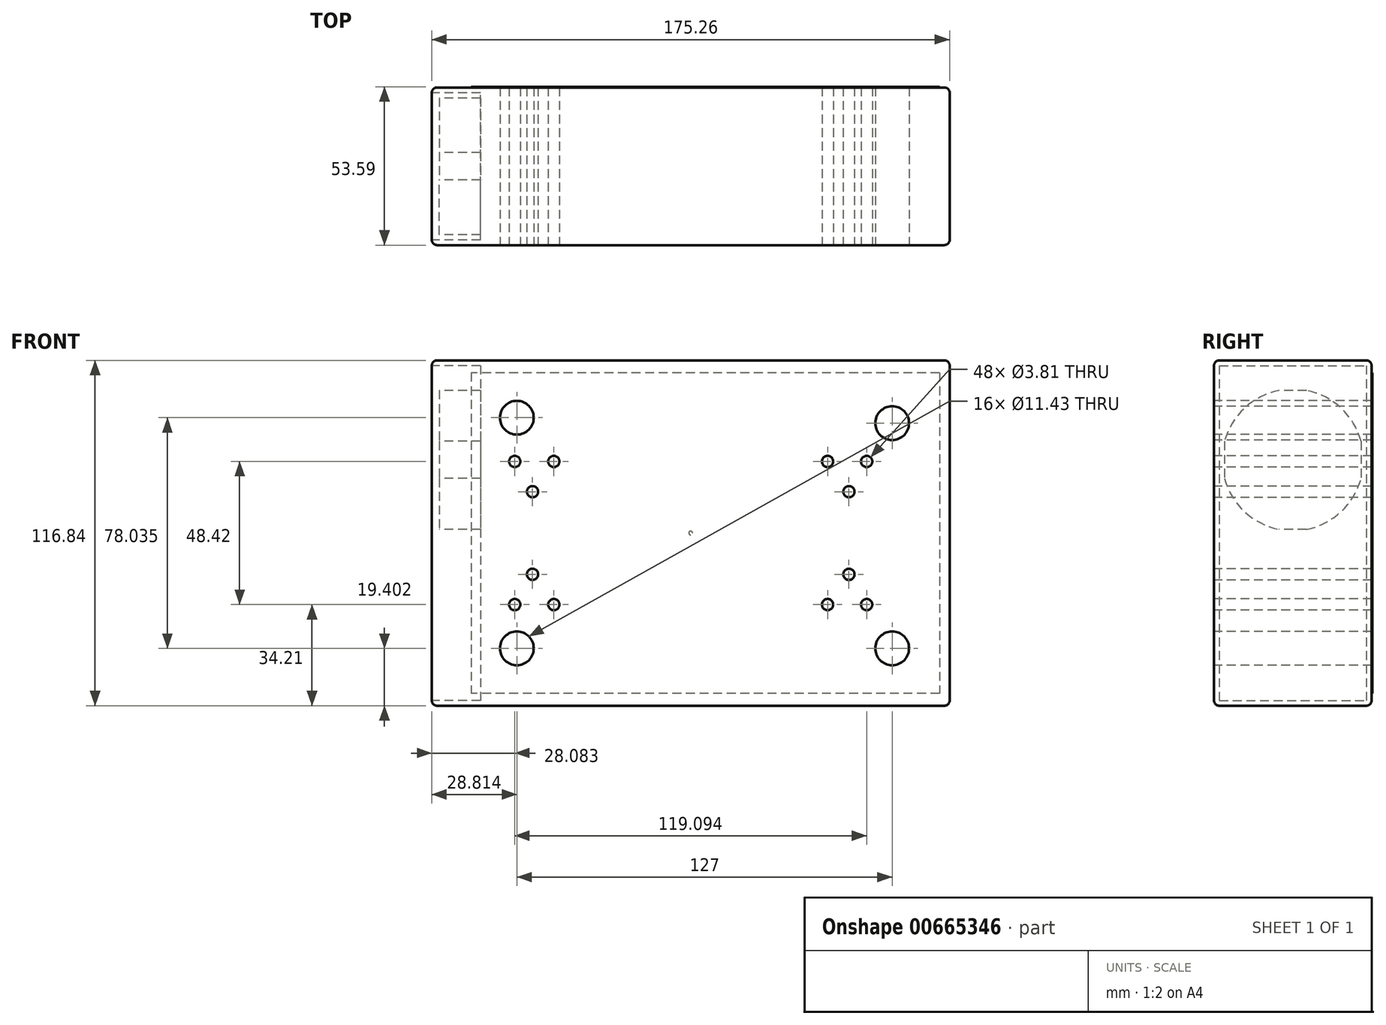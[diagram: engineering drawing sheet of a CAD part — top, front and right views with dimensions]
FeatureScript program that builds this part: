
annotation { "Feature Type Name" : "Feature", "Feature Type Description" : "" }
export const myFeature = defineFeature(function(context is Context, id is Id, definition is map)
    precondition{}
    {
        {
            var Q0;
            Q0=qCreatedBy(makeId("Front.planeOp"),FACE);
            var sketch = newSketch(context, id + "F0", { "sketchPlane" : qUnion([Q0])});
            skLineSegment(sketch, "E0.bottom", {"start": v(-87.63, 58.42) * mm, "end": v(87.63, 58.42) * mm});
            skLineSegment(sketch, "E0.top", {"start": v(-87.63, -58.42) * mm, "end": v(87.63, -58.42) * mm});
            skLineSegment(sketch, "E0.left", {"start": v(-87.63, 58.42) * mm, "end": v(-87.63, -58.42) * mm});
            skLineSegment(sketch, "E0.right", {"start": v(87.63, 58.42) * mm, "end": v(87.63, -58.42) * mm});
            skPoint(sketch, "E0.middle", {"position": v(0, 0) * mm});
            skSolve(sketch);
        }
        {
            var Q0;
            Q0=makeQuery(id+"F0.imprint","IMPRINT",FACE,{"disambiguationData":[TD([[makeQuery(id+"F0.imprint","IMPRINT",EDGE,{"derivedFrom":sQuery(id+"F0.wireOp",EDGE,"E0.bottom")}),-1.0]])]});
            extrude(context, id + "F1", {"entities" : qUnion([Q0]), "depth" : 53.34 * mm});
        }
        {
            var Q0;
            Q0=makeQuery(id+"F1.opExtrude","CAP_FACE",FACE,{"disambiguationData":[OSD([sQuery(id+"F0.wireOp",EDGE,"E0.bottom"),sQuery(id+"F0.wireOp",EDGE,"E0.top"),sQuery(id+"F0.wireOp",EDGE,"E0.left"),sQuery(id+"F0.wireOp",EDGE,"E0.right")])],"isStart":true});
            var sketch = newSketch(context, id + "F2", { "sketchPlane" : qUnion([Q0])});
            skLineSegment(sketch, "E1", {"start": v(-87.63, 54.2) * mm, "end": v(87.63, 54.2) * mm});
            skLineSegment(sketch, "E2.MirrorCS", {"start": v(-87.63, -54.2) * mm, "end": v(87.63, -54.2) * mm});
            skLineSegment(sketch, "E3", {"start": v(74.22, 58.42) * mm, "end": v(74.22, -58.42) * mm});
            skLineSegment(sketch, "E4", {"start": v(-84.2, 54.2) * mm, "end": v(-84.2, -58.42) * mm});
            skCircle(sketch, "E5", {"center": v(0, 0) * mm, "radius": 0.64 * mm});
            skSolve(sketch);
        }
        {
            var Q0;
            Q0=qSketchRegion(id+"F2",true);
            extrude(context, id + "F3", {"entities" : qUnion([Q0]), "depth" : 0.25 * mm});
        }
        {
            var Q0;
            Q0=makeQuery(id+"F1.opExtrude","CAP_FACE",FACE,{"disambiguationData":[OSD([sQuery(id+"F0.wireOp",EDGE,"E0.bottom"),sQuery(id+"F0.wireOp",EDGE,"E0.top"),sQuery(id+"F0.wireOp",EDGE,"E0.left"),sQuery(id+"F0.wireOp",EDGE,"E0.right")])],"isStart":false});
            var sketch = newSketch(context, id + "F4", { "sketchPlane" : qUnion([Q0])});
            skCircle(sketch, "E6", {"center": v(68.18, -39.02) * mm, "radius": 4.35 * mm});
            skCircle(sketch, "E7", {"center": v(-58.82, -39.02) * mm, "radius": 4.87 * mm});
            skCircle(sketch, "E8", {"center": v(68.18, 37.18) * mm, "radius": 4.37 * mm});
            skCircle(sketch, "E9.MirrorC", {"center": v(-58.82, 39.02) * mm, "radius": 4.87 * mm});
            skCircle(sketch, "E10", {"center": v(59.55, -24.2) * mm, "radius": 1.93 * mm});
            skCircle(sketch, "E11", {"center": v(53.53, -13.98) * mm, "radius": 1.7 * mm});
            skCircle(sketch, "E12", {"center": v(46.31, -24.2) * mm, "radius": 1.93 * mm});
            skCircle(sketch, "E13.MirrorC", {"center": v(59.55, 24.2) * mm, "radius": 1.93 * mm});
            skCircle(sketch, "E14.MirrorC", {"center": v(46.31, 24.2) * mm, "radius": 1.93 * mm});
            skCircle(sketch, "E15.MirrorC", {"center": v(53.53, 13.98) * mm, "radius": 1.7 * mm});
            skCircle(sketch, "E16.MirrorC", {"center": v(-46.31, -24.2) * mm, "radius": 1.93 * mm});
            skCircle(sketch, "E17.MirrorC", {"center": v(-59.55, -24.2) * mm, "radius": 1.93 * mm});
            skCircle(sketch, "E18.MirrorC", {"center": v(-53.53, -13.98) * mm, "radius": 1.7 * mm});
            skCircle(sketch, "E19.MirrorC", {"center": v(-46.31, 24.2) * mm, "radius": 1.93 * mm});
            skCircle(sketch, "E20.MirrorC", {"center": v(-53.53, 13.98) * mm, "radius": 1.7 * mm});
            skCircle(sketch, "E21.MirrorC", {"center": v(-59.55, 24.2) * mm, "radius": 1.93 * mm});
            skSolve(sketch);
        }
        {
            var Q0;
            Q0=sQuery(id+"F4.wireOp",VERTEX,"E6.center");
            var Q1;
            Q1=sQuery(id+"F4.wireOp",VERTEX,"E8.center");
            var Q2;
            Q2=sQuery(id+"F4.wireOp",VERTEX,"E7.center");
            var Q3;
            Q3=sQuery(id+"F4.wireOp",VERTEX,"E9.MirrorC.center");
            var Q4;
            Q4=makeQuery(id+"F1.opExtrude","SWEPT_BODY",BODY,{"disambiguationData":[OSD([sQuery(id+"F0.wireOp",EDGE,"E0.bottom"),sQuery(id+"F0.wireOp",EDGE,"E0.top"),sQuery(id+"F0.wireOp",EDGE,"E0.left"),sQuery(id+"F0.wireOp",EDGE,"E0.right")])]});
            var Q5;
            Q5=makeQuery(id+"F3.opExtrude","SWEPT_BODY",BODY,{"disambiguationData":[OSD([sQuery(id+"F2.wireOp",EDGE,"E1"),sQuery(id+"F2.wireOp",EDGE,"E2.MirrorCS"),sQuery(id+"F2.wireOp",EDGE,"E3"),sQuery(id+"F2.wireOp",EDGE,"E4")])]});
            hole(context, id + "F5", {"style" : HoleStyle.SIMPLE, "endStyle" : HoleEndStyle.BLIND_IN_LAST, "holeDiameter" : 11.43 * mm, "tapDrillDiameter" : 11.43 * mm, "holeDepth" : 12.7 * mm, "locations" : qUnion([Q0, Q1, Q2, Q3]), "scope" : qUnion([Q4, Q5])});
        }
        {
            var Q0;
            Q0=sQuery(id+"F4.wireOp",VERTEX,"E10.center");
            var Q1;
            Q1=sQuery(id+"F4.wireOp",VERTEX,"E11.center");
            var Q2;
            Q2=sQuery(id+"F4.wireOp",VERTEX,"E12.center");
            var Q3;
            Q3=sQuery(id+"F4.wireOp",VERTEX,"E15.MirrorC.center");
            var Q4;
            Q4=sQuery(id+"F4.wireOp",VERTEX,"E14.MirrorC.center");
            var Q5;
            Q5=sQuery(id+"F4.wireOp",VERTEX,"E13.MirrorC.center");
            var Q6;
            Q6=sQuery(id+"F4.wireOp",VERTEX,"E18.MirrorC.center");
            var Q7;
            Q7=sQuery(id+"F4.wireOp",VERTEX,"E17.MirrorC.center");
            var Q8;
            Q8=sQuery(id+"F4.wireOp",VERTEX,"E16.MirrorC.center");
            var Q9;
            Q9=sQuery(id+"F4.wireOp",VERTEX,"E20.MirrorC.center");
            var Q10;
            Q10=sQuery(id+"F4.wireOp",VERTEX,"E21.MirrorC.center");
            var Q11;
            Q11=sQuery(id+"F4.wireOp",VERTEX,"E19.MirrorC.center");
            var Q12;
            Q12=makeQuery(id+"F1.opExtrude","SWEPT_BODY",BODY,{"disambiguationData":[OSD([sQuery(id+"F0.wireOp",EDGE,"E0.bottom"),sQuery(id+"F0.wireOp",EDGE,"E0.top"),sQuery(id+"F0.wireOp",EDGE,"E0.left"),sQuery(id+"F0.wireOp",EDGE,"E0.right")])]});
            var Q13;
            Q13=makeQuery(id+"F3.opExtrude","SWEPT_BODY",BODY,{"disambiguationData":[OSD([sQuery(id+"F2.wireOp",EDGE,"E1"),sQuery(id+"F2.wireOp",EDGE,"E2.MirrorCS"),sQuery(id+"F2.wireOp",EDGE,"E3"),sQuery(id+"F2.wireOp",EDGE,"E4")])]});
            hole(context, id + "F6", {"style" : HoleStyle.SIMPLE, "endStyle" : HoleEndStyle.BLIND_IN_LAST, "holeDiameter" : 3.8 * mm, "tapDrillDiameter" : 3.8 * mm, "holeDepth" : 12.7 * mm, "locations" : qUnion([Q0, Q1, Q2, Q3, Q4, Q5, Q6, Q7, Q8, Q9, Q10, Q11]), "scope" : qUnion([Q12, Q13])});
        }
        {
            var Q0;
            Q0=makeQuery(id+"F1.opExtrude","SWEPT_FACE",FACE,{"disambiguationData":[OSD([sQuery(id+"F0.wireOp",EDGE,"E0.left")])]});
            var Q1;
            Q1=makeQuery(id+"F1.opExtrude","SWEPT_FACE",FACE,{"disambiguationData":[OSD([sQuery(id+"F0.wireOp",EDGE,"E0.bottom")])]});
            var Q2;
            Q2=makeQuery(id+"F1.opExtrude","SWEPT_FACE",FACE,{"disambiguationData":[OSD([sQuery(id+"F0.wireOp",EDGE,"E0.right")])]});
            var Q3;
            Q3=makeQuery(id+"F1.opExtrude","SWEPT_FACE",FACE,{"disambiguationData":[OSD([sQuery(id+"F0.wireOp",EDGE,"E0.top")])]});
            fillet(context, id + "F7", {"entities" : qUnion([Q0, Q1, Q2, Q3]), "radius" : 1.78 * mm, "tangentPropagation" : true, "allowEdgeOverflow" : false});
        }
        {
            var Q0;
            Q0=makeQuery(id+"F1.opExtrude","SWEPT_FACE",FACE,{"disambiguationData":[OSD([sQuery(id+"F0.wireOp",EDGE,"E0.left")])]});
            var sketch = newSketch(context, id + "F8", { "sketchPlane" : qUnion([Q0])});
            skLineSegment(sketch, "E22", {"start": v(1.78, 0) * mm, "end": v(51.56, 0) * mm, "construction": true});
            skLineSegment(sketch, "E23", {"start": v(26.67, -56.64) * mm, "end": v(26.67, 56.64) * mm, "construction": true});
            skPoint(sketch, "E24.middle", {"position": v(26.67, -29.91) * mm});
            skArc(sketch, "E25", {"start": v(31.33, -48.24) * mm, "mid": v(43.02, -42.25) * mm, "end": v(49.79, -31.01) * mm});
            skLineSegment(sketch, "E26.bottom", {"start": v(22, -48.24) * mm, "end": v(31.33, -48.24) * mm});
            skLineSegment(sketch, "E26.top", {"start": v(22, -1.25) * mm, "end": v(31.33, -1.25) * mm});
            skLineSegment(sketch, "E26.left", {"start": v(3.55, -31.01) * mm, "end": v(3.55, -18.48) * mm});
            skLineSegment(sketch, "E26.right", {"start": v(49.79, -31.01) * mm, "end": v(49.79, -18.48) * mm});
            skPoint(sketch, "E27.orphan", {"position": v(3.55, -48.24) * mm});
            skPoint(sketch, "E28.orphan", {"position": v(49.79, -48.24) * mm});
            skArc(sketch, "E29.trimOffspring", {"start": v(3.55, -31.01) * mm, "mid": v(10.32, -42.25) * mm, "end": v(22, -48.24) * mm});
            skPoint(sketch, "E30.orphan", {"position": v(3.55, -1.25) * mm});
            skArc(sketch, "E31.trimOffspring", {"start": v(22, -1.25) * mm, "mid": v(10.32, -7.23) * mm, "end": v(3.55, -18.48) * mm});
            skPoint(sketch, "E32.orphan", {"position": v(49.79, -1.25) * mm});
            skArc(sketch, "E33.trimOffspring", {"start": v(49.79, -18.48) * mm, "mid": v(43.02, -7.23) * mm, "end": v(31.33, -1.25) * mm});
            skArc(sketch, "E34.MirrorCS", {"start": v(22, 1.25) * mm, "mid": v(10.32, 7.23) * mm, "end": v(3.55, 18.48) * mm});
            skLineSegment(sketch, "E35.MirrorCS", {"start": v(22, 1.25) * mm, "end": v(31.33, 1.25) * mm});
            skArc(sketch, "E36.MirrorCS", {"start": v(49.79, 18.48) * mm, "mid": v(43.02, 7.23) * mm, "end": v(31.33, 1.25) * mm});
            skLineSegment(sketch, "E37.MirrorCS", {"start": v(49.79, 31.01) * mm, "end": v(49.79, 18.48) * mm});
            skArc(sketch, "E38.MirrorCS", {"start": v(31.33, 48.24) * mm, "mid": v(43.02, 42.25) * mm, "end": v(49.79, 31.01) * mm});
            skLineSegment(sketch, "E39.MirrorCS", {"start": v(22, 48.24) * mm, "end": v(31.33, 48.24) * mm});
            skArc(sketch, "E40.MirrorCS", {"start": v(3.55, 31.01) * mm, "mid": v(10.32, 42.25) * mm, "end": v(22, 48.24) * mm});
            skLineSegment(sketch, "E41.MirrorCS", {"start": v(3.55, 31.01) * mm, "end": v(3.55, 18.48) * mm});
            skSolve(sketch);
        }
        {
            var Q0;
            Q0=makeQuery(id+"F8.imprint","IMPRINT",FACE,{"disambiguationData":[TD([[makeQuery(id+"F8.imprint","IMPRINT",EDGE,{"derivedFrom":sQuery(id+"F8.wireOp",EDGE,"E25")}),1.0]])]});
            var Q1;
            Q1=makeQuery(id+"F8.imprint","IMPRINT",FACE,{"disambiguationData":[TD([[makeQuery(id+"F8.imprint","IMPRINT",EDGE,{"derivedFrom":sQuery(id+"F8.wireOp",EDGE,"E34.MirrorCS")}),-1.0]])]});
            extrude(context, id + "F9", {"entities" : qUnion([Q0, Q1]), "operationType" : NewBodyOperationType.REMOVE, "oppositeDirection" : true, "depth" : 16.5 * mm});
        }
        {
            var Q0;
            Q0=makeQuery(id+"F1.opExtrude","SWEPT_FACE",FACE,{"disambiguationData":[OSD([sQuery(id+"F0.wireOp",EDGE,"E0.left")])]});
            var sketch = newSketch(context, id + "F10", { "sketchPlane" : qUnion([Q0])});
            skCircle(sketch, "E42", {"center": v(8.88, -51.96) * mm, "radius": 3.43 * mm});
            skLineSegment(sketch, "E43.0", {"start": v(7.32, -51.96) * mm, "end": v(8.1, -50.6) * mm});
            skLineSegment(sketch, "E43.1", {"start": v(8.1, -50.6) * mm, "end": v(9.74, -50.57) * mm});
            skLineSegment(sketch, "E43.2", {"start": v(9.74, -50.57) * mm, "end": v(10.52, -51.92) * mm});
            skLineSegment(sketch, "E43.3", {"start": v(10.52, -51.92) * mm, "end": v(9.67, -53.32) * mm});
            skLineSegment(sketch, "E43.4", {"start": v(9.67, -53.32) * mm, "end": v(8.1, -53.32) * mm});
            skLineSegment(sketch, "E43.5", {"start": v(8.1, -53.32) * mm, "end": v(7.32, -51.96) * mm});
            skLineSegment(sketch, "E44", {"start": v(1.78, 0) * mm, "end": v(51.56, 0) * mm, "construction": true});
            skLineSegment(sketch, "E45", {"start": v(26.67, -56.64) * mm, "end": v(26.67, 56.64) * mm, "construction": true});
            skLineSegment(sketch, "E46.MirrorCS", {"start": v(9.67, 53.32) * mm, "end": v(8.1, 53.32) * mm});
            skLineSegment(sketch, "E47.MirrorCS", {"start": v(8.1, 53.32) * mm, "end": v(7.32, 51.96) * mm});
            skLineSegment(sketch, "E48.MirrorCS", {"start": v(9.74, 50.57) * mm, "end": v(10.52, 51.92) * mm});
            skLineSegment(sketch, "E49.MirrorCS", {"start": v(10.52, 51.92) * mm, "end": v(9.67, 53.32) * mm});
            skLineSegment(sketch, "E50.MirrorCS", {"start": v(8.1, 50.6) * mm, "end": v(9.74, 50.57) * mm});
            skLineSegment(sketch, "E51.MirrorCS", {"start": v(7.32, 51.96) * mm, "end": v(8.1, 50.6) * mm});
            skCircle(sketch, "E52.MirrorC", {"center": v(8.88, 51.96) * mm, "radius": 3.43 * mm});
            skLineSegment(sketch, "E53.MirrorCS", {"start": v(46.02, -51.96) * mm, "end": v(45.24, -50.6) * mm});
            skLineSegment(sketch, "E54.MirrorCS", {"start": v(45.24, -50.6) * mm, "end": v(43.6, -50.57) * mm});
            skLineSegment(sketch, "E55.MirrorCS", {"start": v(45.24, -53.32) * mm, "end": v(46.02, -51.96) * mm});
            skLineSegment(sketch, "E56.MirrorCS", {"start": v(42.82, -51.92) * mm, "end": v(43.67, -53.32) * mm});
            skLineSegment(sketch, "E57.MirrorCS", {"start": v(43.6, -50.57) * mm, "end": v(42.82, -51.92) * mm});
            skLineSegment(sketch, "E58.MirrorCS", {"start": v(43.67, -53.32) * mm, "end": v(45.24, -53.32) * mm});
            skCircle(sketch, "E59.MirrorC", {"center": v(44.46, -51.96) * mm, "radius": 3.43 * mm});
            skLineSegment(sketch, "E60.MirrorCS", {"start": v(46.02, 51.96) * mm, "end": v(45.24, 50.6) * mm});
            skLineSegment(sketch, "E61.MirrorCS", {"start": v(45.24, 53.32) * mm, "end": v(46.02, 51.96) * mm});
            skCircle(sketch, "E62.MirrorC", {"center": v(44.46, 51.96) * mm, "radius": 3.43 * mm});
            skLineSegment(sketch, "E63.MirrorCS", {"start": v(45.24, 50.6) * mm, "end": v(43.6, 50.57) * mm});
            skLineSegment(sketch, "E64.MirrorCS", {"start": v(43.6, 50.57) * mm, "end": v(42.82, 51.92) * mm});
            skLineSegment(sketch, "E65.MirrorCS", {"start": v(42.82, 51.92) * mm, "end": v(43.67, 53.32) * mm});
            skLineSegment(sketch, "E66.MirrorCS", {"start": v(43.67, 53.32) * mm, "end": v(45.24, 53.32) * mm});
            skSolve(sketch);
        }
        {
            var Q0;
            Q0=makeQuery(id+"F10.imprint","IMPRINT",FACE,{"disambiguationData":[TD([[makeQuery(id+"F10.imprint","IMPRINT",EDGE,{"derivedFrom":sQuery(id+"F10.wireOp",EDGE,"E42")}),1.0]])]});
            var Q1;
            Q1=makeQuery(id+"F10.imprint","IMPRINT",FACE,{"disambiguationData":[TD([[makeQuery(id+"F10.imprint","IMPRINT",EDGE,{"derivedFrom":sQuery(id+"F10.wireOp",EDGE,"E53.MirrorCS")}),-1.0]])]});
            var Q2;
            Q2=makeQuery(id+"F10.imprint","IMPRINT",FACE,{"disambiguationData":[TD([[makeQuery(id+"F10.imprint","IMPRINT",EDGE,{"derivedFrom":sQuery(id+"F10.wireOp",EDGE,"E60.MirrorCS")}),1.0]])]});
            var Q3;
            Q3=makeQuery(id+"F10.imprint","IMPRINT",FACE,{"disambiguationData":[TD([[makeQuery(id+"F10.imprint","IMPRINT",EDGE,{"derivedFrom":sQuery(id+"F10.wireOp",EDGE,"E46.MirrorCS")}),-1.0]])]});
            var Q4;
            Q4=sQuery(id+"F10.wireOp",EDGE,"E42");
            var Q5;
            Q5=sQuery(id+"F10.wireOp",EDGE,"E52.MirrorC");
            var Q6;
            Q6=sQuery(id+"F10.wireOp",EDGE,"E62.MirrorC");
            var Q7;
            Q7=sQuery(id+"F10.wireOp",EDGE,"E59.MirrorC");
            extrude(context, id + "F11", {"entities" : qUnion([Q0, Q1, Q2, Q3]), "operationType" : NewBodyOperationType.REMOVE, "surfaceEntities" : qUnion([Q4, Q5, Q6, Q7]), "oppositeDirection" : true, "depth" : 1.02 * mm});
        }
        {
            var Q0;
            Q0=makeQuery(id+"F11.boolean.opBoolean","SPLIT",FACE,{"disambiguationData":[TD([makeQuery(id+"F11.opExtrude","SWEPT_FACE",FACE,{"disambiguationData":[OSD([sQuery(id+"F10.wireOp",EDGE,"E43.0")])]})])],"derivedFrom":makeQuery(id+"F1.opExtrude","SWEPT_FACE",FACE,{"disambiguationData":[OSD([sQuery(id+"F0.wireOp",EDGE,"E0.left")])]})});
            var Q1;
            Q1=makeQuery(id+"F11.boolean.opBoolean","SPLIT",FACE,{"disambiguationData":[TD([makeQuery(id+"F11.opExtrude","SWEPT_FACE",FACE,{"disambiguationData":[OSD([sQuery(id+"F10.wireOp",EDGE,"E53.MirrorCS")])]})])],"derivedFrom":makeQuery(id+"F1.opExtrude","SWEPT_FACE",FACE,{"disambiguationData":[OSD([sQuery(id+"F0.wireOp",EDGE,"E0.left")])]})});
            var Q2;
            Q2=makeQuery(id+"F11.boolean.opBoolean","SPLIT",FACE,{"disambiguationData":[TD([makeQuery(id+"F11.opExtrude","SWEPT_FACE",FACE,{"disambiguationData":[OSD([sQuery(id+"F10.wireOp",EDGE,"E46.MirrorCS")])]})])],"derivedFrom":makeQuery(id+"F1.opExtrude","SWEPT_FACE",FACE,{"disambiguationData":[OSD([sQuery(id+"F0.wireOp",EDGE,"E0.left")])]})});
            var Q3;
            Q3=makeQuery(id+"F11.boolean.opBoolean","SPLIT",FACE,{"disambiguationData":[TD([makeQuery(id+"F11.opExtrude","SWEPT_FACE",FACE,{"disambiguationData":[OSD([sQuery(id+"F10.wireOp",EDGE,"E60.MirrorCS")])]})])],"derivedFrom":makeQuery(id+"F1.opExtrude","SWEPT_FACE",FACE,{"disambiguationData":[OSD([sQuery(id+"F0.wireOp",EDGE,"E0.left")])]})});
            extrude(context, id + "F12", {"entities" : qUnion([Q0, Q1, Q2, Q3]), "operationType" : NewBodyOperationType.REMOVE, "oppositeDirection" : true, "depth" : 2.54 * mm});
        }
        {
            var Q0;
            Q0=makeQuery(id+"F3.opExtrude","SWEPT_BODY",BODY,{"disambiguationData":[OSD([sQuery(id+"F2.wireOp",EDGE,"E1"),sQuery(id+"F2.wireOp",EDGE,"E2.MirrorCS"),sQuery(id+"F2.wireOp",EDGE,"E3"),sQuery(id+"F2.wireOp",EDGE,"E4"),sQuery(id+"F2.wireOp",EDGE,"E5")])]});
            transform(context, id + "F13", {"entities" : qUnion([Q0]), "transformType" : TransformType.TRANSLATION_3D, "dx" : 0 * mm, "dy" : 0 * mm, "dz" : 0 * mm, "makeCopy" : true});
        }
        {
            var Q0;
            Q0=makeQuery(id+"F13.opPattern","COPY",BODY,{"derivedFrom":makeQuery(id+"F3.opExtrude","SWEPT_BODY",BODY,{"disambiguationData":[OSD([sQuery(id+"F2.wireOp",EDGE,"E1"),sQuery(id+"F2.wireOp",EDGE,"E2.MirrorCS"),sQuery(id+"F2.wireOp",EDGE,"E3"),sQuery(id+"F2.wireOp",EDGE,"E4"),sQuery(id+"F2.wireOp",EDGE,"E5")])]}),"instanceName":"1"});
            deleteBodies(context, id + "F14", {"entities" : qUnion([Q0])});
        }
    });
